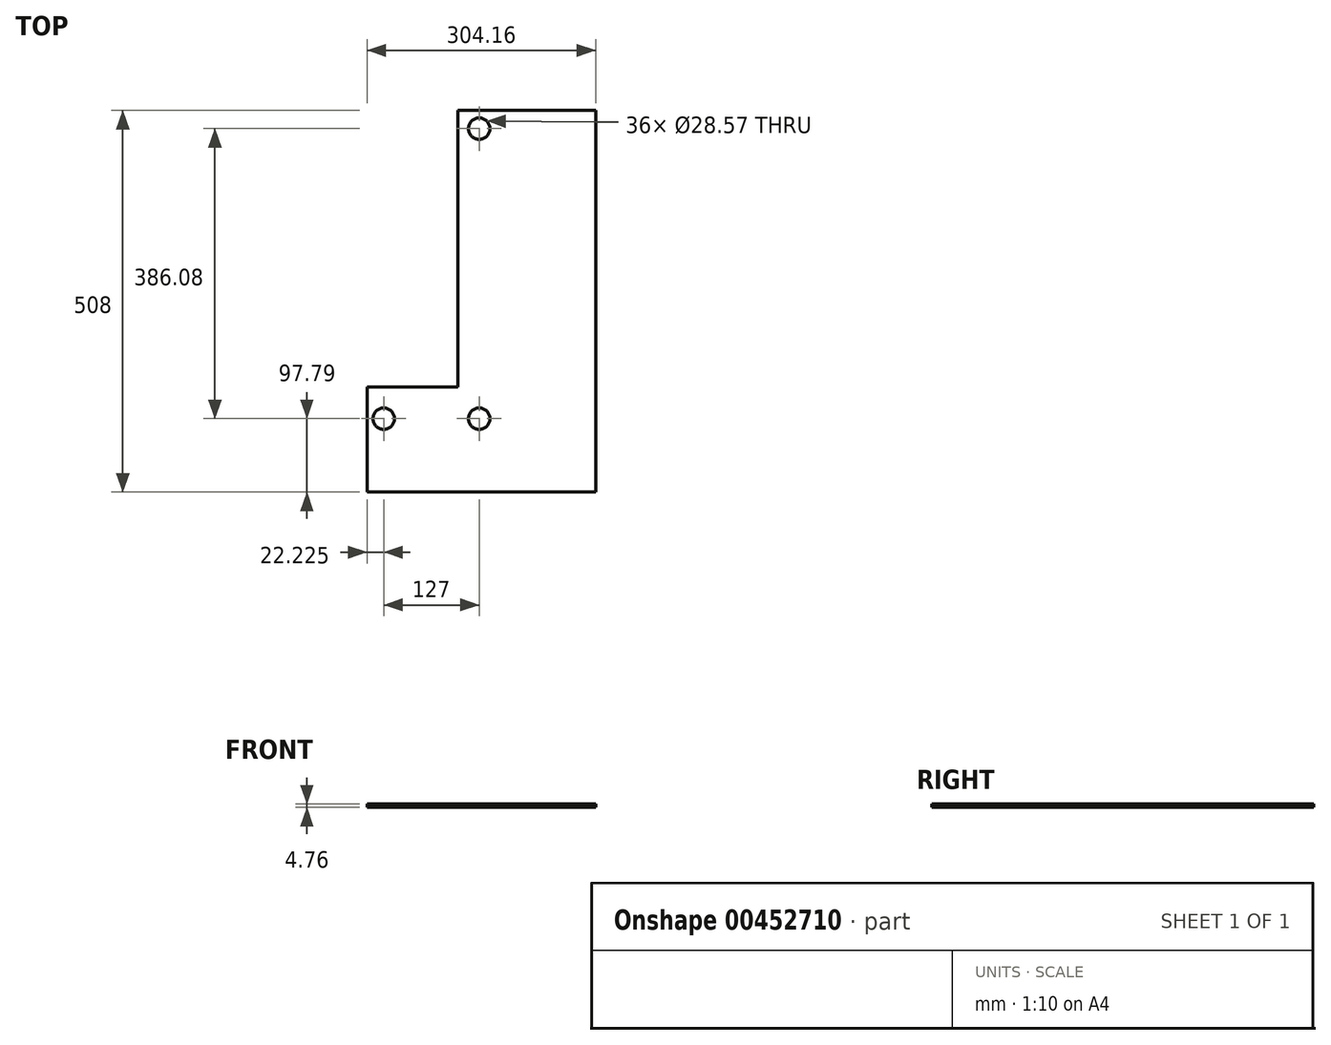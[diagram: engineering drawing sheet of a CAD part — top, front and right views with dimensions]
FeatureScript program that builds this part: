
annotation { "Feature Type Name" : "Feature", "Feature Type Description" : "" }
export const myFeature = defineFeature(function(context is Context, id is Id, definition is map)
    precondition{}
    {
        {
            var Q0;
            Q0=qCreatedBy(makeId("Top.planeOp"),FACE);
            var sketch = newSketch(context, id + "F0", { "sketchPlane" : qUnion([Q0])});
            skLineSegment(sketch, "E0.bottom", {"start": v(-101.6, 254) * mm, "end": v(101.6, 254) * mm});
            skLineSegment(sketch, "E0.top", {"start": v(-101.6, -254) * mm, "end": v(101.6, -254) * mm});
            skLineSegment(sketch, "E0.left", {"start": v(-101.6, 254) * mm, "end": v(-101.6, -254) * mm});
            skLineSegment(sketch, "E0.right", {"start": v(101.6, 254) * mm, "end": v(101.6, -254) * mm});
            skPoint(sketch, "E0.middle", {"position": v(0, 0) * mm});
            skCircle(sketch, "E1", {"center": v(47.63, -156.2) * mm, "radius": 14.29 * mm});
            skCircle(sketch, "E2", {"center": v(-79.37, -156.2) * mm, "radius": 14.29 * mm});
            skCircle(sketch, "E3", {"center": v(47.62, 229.87) * mm, "radius": 14.29 * mm});
            skLineSegment(sketch, "E4.bottom", {"start": v(101.6, 254) * mm, "end": v(202.56, 254) * mm});
            skLineSegment(sketch, "E4.top", {"start": v(101.6, -254) * mm, "end": v(202.57, -254) * mm});
            skLineSegment(sketch, "E4.right", {"start": v(202.56, 254) * mm, "end": v(202.57, -254) * mm});
            skLineSegment(sketch, "E5", {"start": v(-101.6, -114.3) * mm, "end": v(101.6, -114.3) * mm});
            skLineSegment(sketch, "E6", {"start": v(19.05, 254) * mm, "end": v(19.05, -114.3) * mm});
            skSolve(sketch);
        }
        {
            var Q0;
            {var subQ2=sQuery(id+"F0.wireOp",EDGE,"E0.top");Q0=makeQuery(id+"F0.imprint","IMPRINT",FACE,{"disambiguationData":[TD([[makeQuery(id+"F0.imprint","IMPRINT",EDGE,{"derivedFrom":subQ2}),1.0]])]});}
            var Q1;
            {var subQ3=sQuery(id+"F0.wireOp",EDGE,"I4vepFfu-DtgQ-1hAy-3Aza-c7Z9ObNEMtMZ");Q1=makeQuery(id+"F0.imprint","IMPRINT",FACE,{"disambiguationData":[TD([[makeQuery(id+"F0.imprint","IMPRINT",EDGE,{"derivedFrom":subQ3}),-1.0]])]});}
            var Q2;
            {var subQ3=sQuery(id+"F0.wireOp",EDGE,"E4.bottom");Q2=makeQuery(id+"F0.imprint","IMPRINT",FACE,{"disambiguationData":[TD([[makeQuery(id+"F0.imprint","IMPRINT",EDGE,{"derivedFrom":subQ3}),-1.0]])]});}
            var Q3;
            Q3=makeQuery(id+"F0.imprint","IMPRINT",FACE,{"disambiguationData":[TD([[makeQuery(id+"F0.imprint","IMPRINT",EDGE,{"derivedFrom":sQuery(id+"F0.wireOp",EDGE,"E3")}),-1.0]])]});
            extrude(context, id + "F1", {"entities" : qUnion([Q0, Q1, Q2, Q3]), "depth" : 4.76 * mm});
        }
    });
